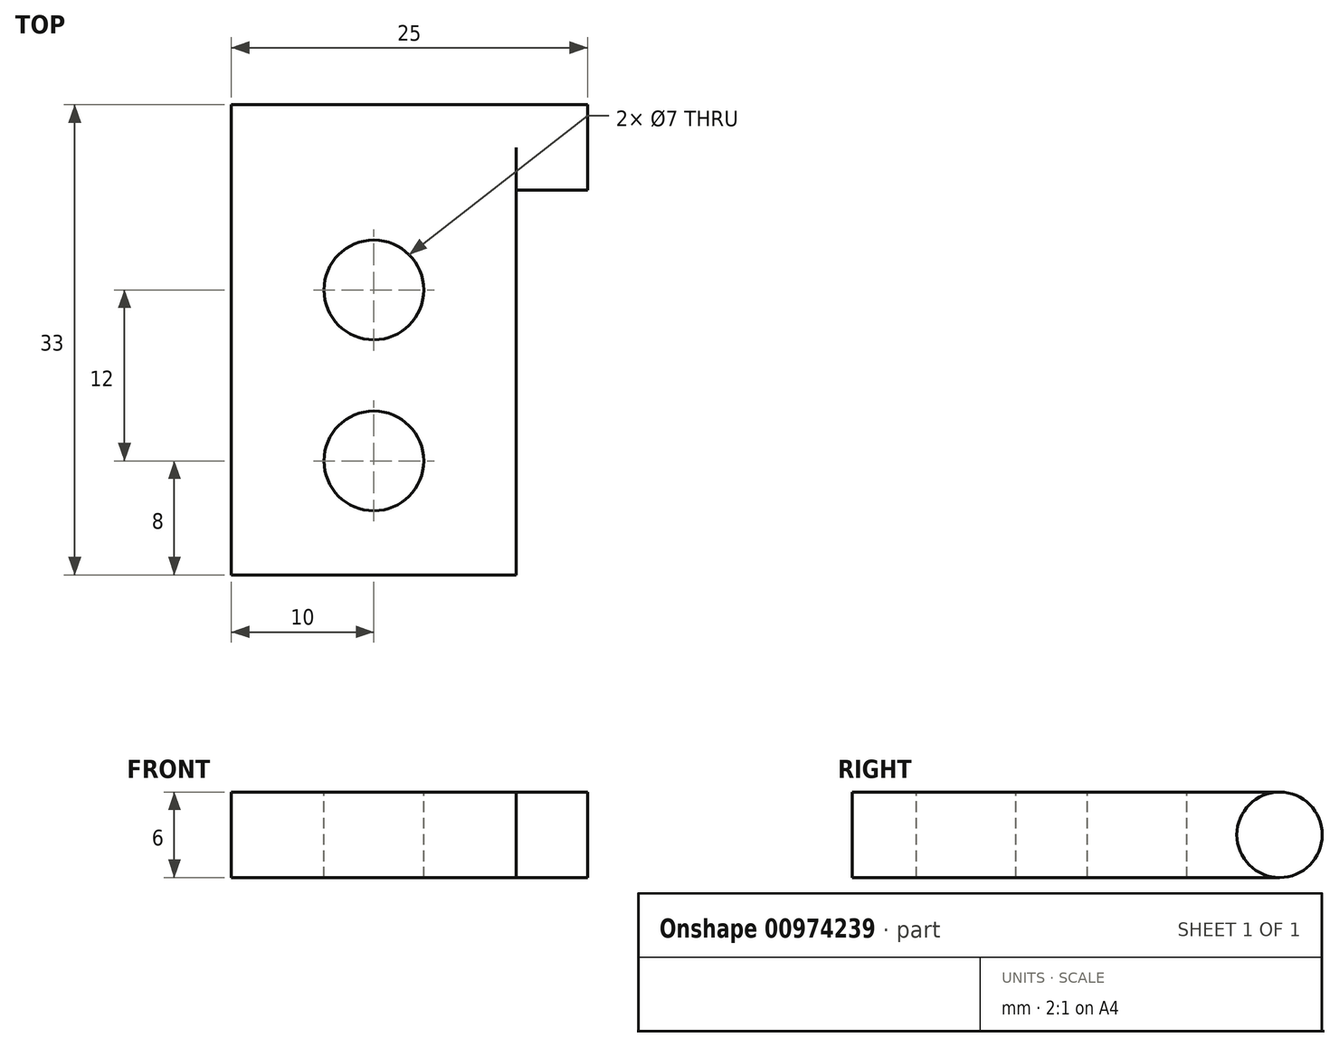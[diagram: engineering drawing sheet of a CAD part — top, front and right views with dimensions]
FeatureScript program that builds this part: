
annotation { "Feature Type Name" : "Feature", "Feature Type Description" : "" }
export const myFeature = defineFeature(function(context is Context, id is Id, definition is map)
    precondition{}
    {
        {
            var Q0;
            Q0=qCreatedBy(makeId("Right.planeOp"),FACE);
            var sketch = newSketch(context, id + "F0", { "sketchPlane" : qUnion([Q0])});
            skLineSegment(sketch, "E0.bottom", {"start": v(-30, 3) * mm, "end": v(0, 3) * mm});
            skLineSegment(sketch, "E0.top", {"start": v(-30, -3) * mm, "end": v(0, -3) * mm});
            skLineSegment(sketch, "E0.left", {"start": v(-30, 3) * mm, "end": v(-30, -3) * mm});
            skLineSegment(sketch, "E0.right", {"start": v(0, 3) * mm, "end": v(0, -3) * mm});
            skCircle(sketch, "E1", {"center": v(0, 0) * mm, "radius": 3 * mm});
            skSolve(sketch);
        }
        {
            var Q0;
            Q0 = qSketchRegion(id + "F0", true);
            extrude(context, id + "F1", {"entities" : qUnion([Q0]), "endBound" : BoundingType.SYMMETRIC, "depth" : 20 * mm, "offsetDistance" : 25 * mm});
        }
        {
            var Q0;
            Q0=makeQuery(id+"F1.opExtrude","CAP_FACE",FACE,{"disambiguationData":[OSD([sQuery(id+"F0.wireOp",EDGE,"E0.bottom"),sQuery(id+"F0.wireOp",EDGE,"E0.top"),sQuery(id+"F0.wireOp",EDGE,"E0.left"),sQuery(id+"F0.wireOp",EDGE,"E1")])],"isStart":false});
            var sketch = newSketch(context, id + "F2", { "sketchPlane" : qUnion([Q0])});
            skCircle(sketch, "E2", {"center": v(0, 0) * mm, "radius": 3 * mm});
            skSolve(sketch);
        }
        {
            var Q0;
            Q0 = qSketchRegion(id + "F2", true);
            extrude(context, id + "F3", {"entities" : qUnion([Q0]), "operationType" : NewBodyOperationType.ADD, "depth" : 5 * mm, "offsetDistance" : 25 * mm});
        }
        {
            var Q0;
            Q0=makeQuery(id+"F1.opExtrude","SWEPT_FACE",FACE,{"disambiguationData":[OSD([sQuery(id+"F0.wireOp",EDGE,"E0.bottom")])]});
            var sketch = newSketch(context, id + "F4", { "sketchPlane" : qUnion([Q0])});
            skCircle(sketch, "E3", {"center": v(0, -10) * mm, "radius": 3.5 * mm});
            skCircle(sketch, "E4", {"center": v(0, -22) * mm, "radius": 3.5 * mm});
            skSolve(sketch);
        }
        {
            var Q0;
            Q0 = qSketchRegion(id + "F4", true);
            extrude(context, id + "F5", {"entities" : qUnion([Q0]), "operationType" : NewBodyOperationType.REMOVE, "endBound" : BoundingType.THROUGH_ALL, "oppositeDirection" : true, "depth" : 25 * mm, "offsetDistance" : 25 * mm});
        }
    });
